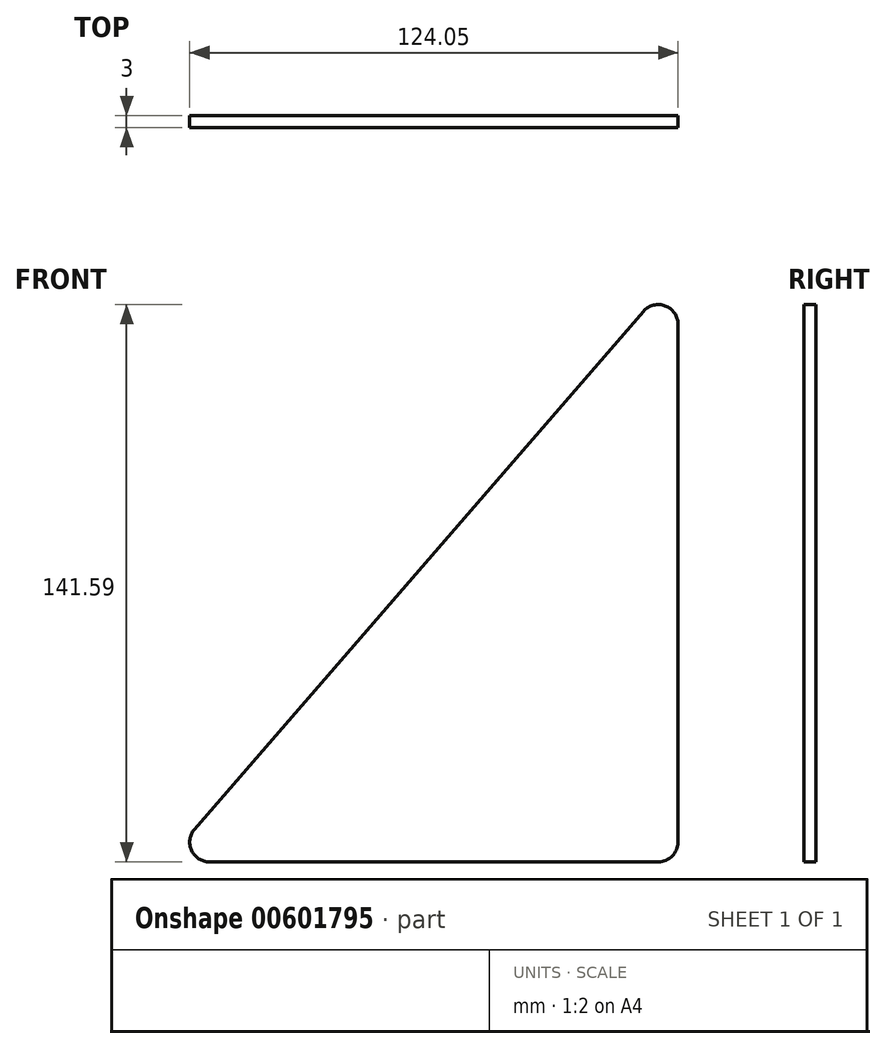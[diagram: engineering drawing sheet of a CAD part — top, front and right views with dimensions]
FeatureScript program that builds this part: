
annotation { "Feature Type Name" : "Feature", "Feature Type Description" : "" }
export const myFeature = defineFeature(function(context is Context, id is Id, definition is map)
    precondition{}
    {
        {
            var Q0;
            Q0=qCreatedBy(makeId("Front.planeOp"),FACE);
            var sketch = newSketch(context, id + "F0", { "sketchPlane" : qUnion([Q0])});
            skLineSegment(sketch, "E0", {"start": v(21.31, 77.56) * mm, "end": v(21.31, -72.44) * mm});
            skLineSegment(sketch, "E1", {"start": v(21.31, -72.44) * mm, "end": v(-108.69, -72.44) * mm});
            skLineSegment(sketch, "E2", {"start": v(-108.69, -72.44) * mm, "end": v(21.31, 77.56) * mm});
            skSolve(sketch);
        }
        {
            var Q0;
            Q0 = qSketchRegion(id + "F0", true);
            extrude(context, id + "F1", {"entities" : qUnion([Q0]), "depth" : 3 * mm, "offsetDistance" : 25 * mm});
        }
        {
            var Q0;
            Q0=makeQuery(id+"F1.opExtrude","SWEPT_EDGE",EDGE,{"disambiguationData":[OSD([sQuery(id+"F0.wireOp",EDGE,"E0"),sQuery(id+"F0.wireOp",EDGE,"E2")])]});
            fillet(context, id + "F2", {"entities" : qUnion([Q0]), "radius" : 5 * mm, "tangentPropagation" : true, "allowEdgeOverflow" : false});
        }
        {
            var Q0;
            Q0=makeQuery(id+"F1.opExtrude","SWEPT_EDGE",EDGE,{"disambiguationData":[OSD([sQuery(id+"F0.wireOp",EDGE,"E0"),sQuery(id+"F0.wireOp",EDGE,"E1")])]});
            fillet(context, id + "F3", {"entities" : qUnion([Q0]), "radius" : 5 * mm, "tangentPropagation" : true, "allowEdgeOverflow" : false});
        }
        {
            var Q0;
            Q0=makeQuery(id+"F1.opExtrude","SWEPT_EDGE",EDGE,{"disambiguationData":[OSD([sQuery(id+"F0.wireOp",EDGE,"E1"),sQuery(id+"F0.wireOp",EDGE,"E2")])]});
            fillet(context, id + "F4", {"entities" : qUnion([Q0]), "radius" : 5 * mm, "tangentPropagation" : true, "allowEdgeOverflow" : false});
        }
    });
